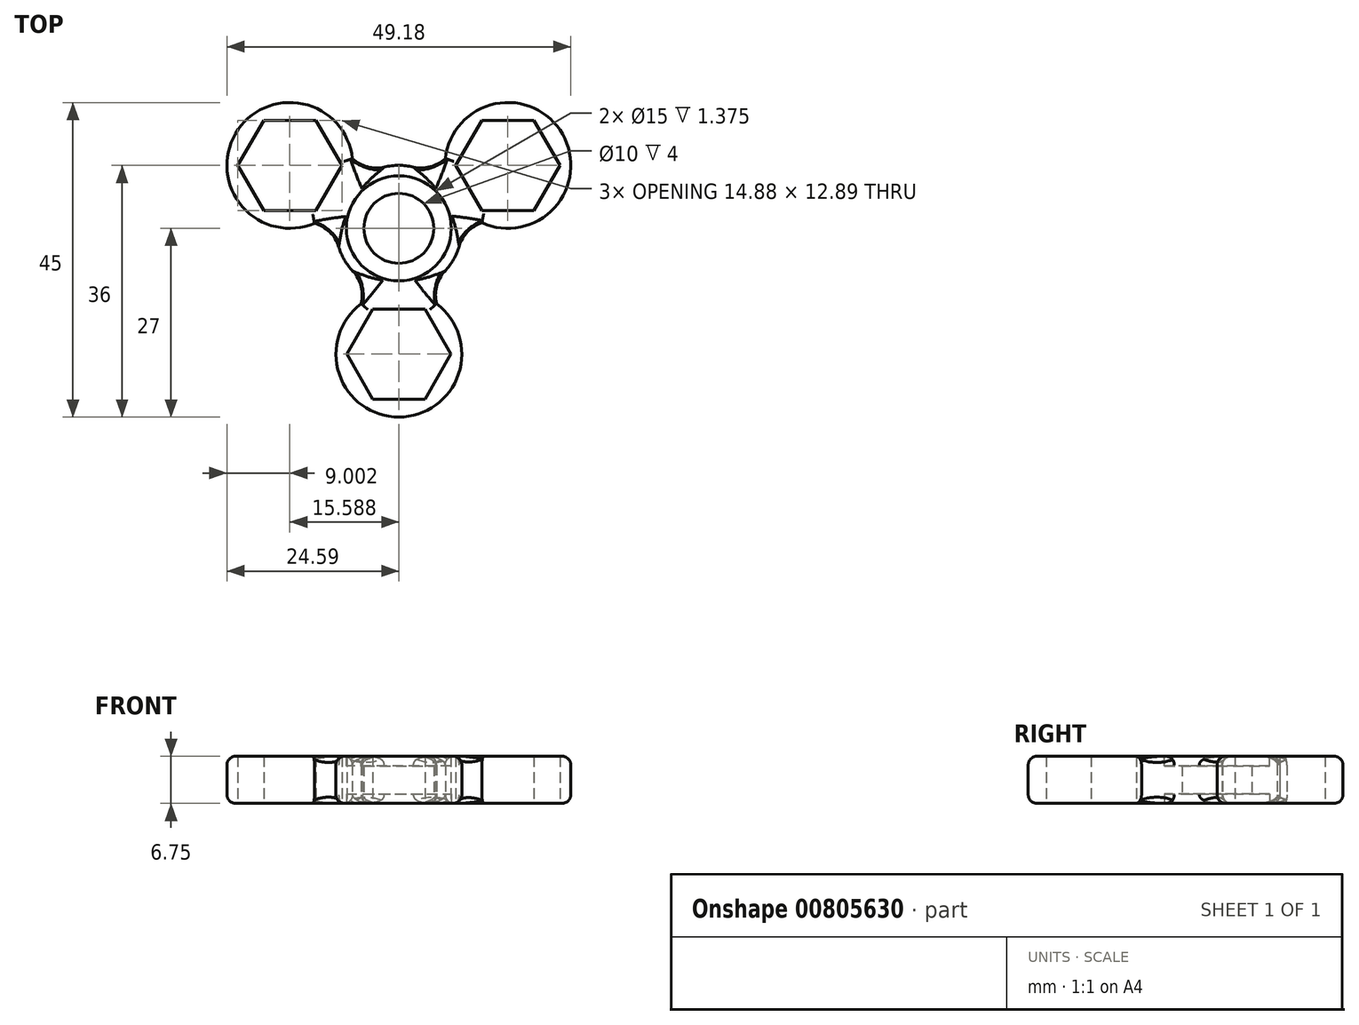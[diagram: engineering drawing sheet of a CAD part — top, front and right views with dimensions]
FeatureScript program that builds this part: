
annotation { "Feature Type Name" : "Feature", "Feature Type Description" : "" }
export const myFeature = defineFeature(function(context is Context, id is Id, definition is map)
    precondition{}
    {
        {
            var Q0;
            Q0=qCreatedBy(makeId("Top.planeOp"),FACE);
            var sketch = newSketch(context, id + "F0", { "sketchPlane" : qUnion([Q0])});
            skCircle(sketch, "E0.cCircle", {"center": v(0, 0) * mm, "radius": 9 * mm, "construction": true});
            skPoint(sketch, "E0.0.midPoint", {"position": v(0, 9) * mm});
            skCircle(sketch, "E1.cCircle", {"center": v(-15.59, 9) * mm, "radius": 6.44 * mm, "construction": true});
            skLineSegment(sketch, "E1.0", {"start": v(-19.3, 15.45) * mm, "end": v(-11.87, 15.45) * mm});
            skLineSegment(sketch, "E1.1", {"start": v(-11.87, 15.45) * mm, "end": v(-8.15, 9) * mm});
            skLineSegment(sketch, "E1.2", {"start": v(-8.15, 9) * mm, "end": v(-11.87, 2.55) * mm});
            skLineSegment(sketch, "E1.3", {"start": v(-11.87, 2.56) * mm, "end": v(-19.3, 2.56) * mm});
            skLineSegment(sketch, "E1.4", {"start": v(-19.3, 2.55) * mm, "end": v(-23.03, 9) * mm});
            skLineSegment(sketch, "E1.5", {"start": v(-23.03, 9) * mm, "end": v(-19.3, 15.45) * mm});
            skPoint(sketch, "E1.0.midPoint", {"position": v(-15.59, 15.45) * mm});
            skCircle(sketch, "E2.cCircle", {"center": v(15.59, 9) * mm, "radius": 6.44 * mm, "construction": true});
            skLineSegment(sketch, "E2.0", {"start": v(11.87, 2.55) * mm, "end": v(8.15, 9) * mm});
            skLineSegment(sketch, "E2.1", {"start": v(8.15, 9) * mm, "end": v(11.87, 15.45) * mm});
            skLineSegment(sketch, "E2.2", {"start": v(11.87, 15.45) * mm, "end": v(19.3, 15.45) * mm});
            skLineSegment(sketch, "E2.3", {"start": v(19.3, 15.45) * mm, "end": v(23.03, 9) * mm});
            skLineSegment(sketch, "E2.4", {"start": v(23.03, 9) * mm, "end": v(19.3, 2.56) * mm});
            skLineSegment(sketch, "E2.5", {"start": v(19.3, 2.56) * mm, "end": v(11.87, 2.55) * mm});
            skPoint(sketch, "E2.0.midPoint", {"position": v(10, 5.78) * mm});
            skCircle(sketch, "E3.cCircle", {"center": v(0, -18) * mm, "radius": 6.45 * mm, "construction": true});
            skLineSegment(sketch, "E3.0", {"start": v(-3.72, -11.56) * mm, "end": v(3.72, -11.56) * mm});
            skLineSegment(sketch, "E3.1", {"start": v(3.72, -11.55) * mm, "end": v(7.44, -18) * mm});
            skLineSegment(sketch, "E3.2", {"start": v(7.44, -18) * mm, "end": v(3.72, -24.44) * mm});
            skLineSegment(sketch, "E3.3", {"start": v(3.72, -24.45) * mm, "end": v(-3.72, -24.45) * mm});
            skLineSegment(sketch, "E3.4", {"start": v(-3.72, -24.45) * mm, "end": v(-7.44, -18) * mm});
            skLineSegment(sketch, "E3.5", {"start": v(-7.44, -18) * mm, "end": v(-3.72, -11.56) * mm});
            skPoint(sketch, "E3.0.midPoint", {"position": v(0, -11.56) * mm});
            skCircle(sketch, "E4", {"center": v(0, 0) * mm, "radius": 5 * mm});
            skLineSegment(sketch, "E5", {"start": v(-15.59, 9) * mm, "end": v(0, 0) * mm, "construction": true});
            skLineSegment(sketch, "E6", {"start": v(0, 0) * mm, "end": v(15.59, 9) * mm, "construction": true});
            skLineSegment(sketch, "E7", {"start": v(0, 0) * mm, "end": v(0, -18) * mm, "construction": true});
            skLineSegment(sketch, "E8", {"start": v(-20.06, 1.2) * mm, "end": v(0, 0) * mm, "construction": true});
            skLineSegment(sketch, "E9", {"start": v(0, 0) * mm, "end": v(-9, -18) * mm, "construction": true});
            skLineSegment(sketch, "E10", {"start": v(9, -18) * mm, "end": v(0, 0) * mm, "construction": true});
            skLineSegment(sketch, "E11", {"start": v(0, 0) * mm, "end": v(20.36, 1.37) * mm, "construction": true});
            skLineSegment(sketch, "E12", {"start": v(11.2, 16.86) * mm, "end": v(0, 0) * mm, "construction": true});
            skLineSegment(sketch, "E13", {"start": v(0, 0) * mm, "end": v(-11.22, 16.87) * mm, "construction": true});
            skLineSegment(sketch, "E14", {"start": v(-12.07, 0.72) * mm, "end": v(-8.98, 0.53) * mm});
            skLineSegment(sketch, "E15", {"start": v(-4.02, -8.05) * mm, "end": v(-5.4, -10.8) * mm});
            skLineSegment(sketch, "E16", {"start": v(4.02, -8.05) * mm, "end": v(5.4, -10.8) * mm});
            skLineSegment(sketch, "E17", {"start": v(8.98, 0.6) * mm, "end": v(11.88, 0.8) * mm});
            skLineSegment(sketch, "E18", {"start": v(4.98, 7.5) * mm, "end": v(6.64, 10) * mm});
            skLineSegment(sketch, "E19", {"start": v(-4.98, 7.5) * mm, "end": v(-6.64, 9.99) * mm});
            skArc(sketch, "E20", {"start": v(4.98, 7.5) * mm, "mid": v(0, 9) * mm, "end": v(-4.98, 7.5) * mm});
            skArc(sketch, "E21", {"start": v(8.98, 0.6) * mm, "mid": v(7.81, -4.47) * mm, "end": v(4.02, -8.05) * mm});
            skArc(sketch, "E22", {"start": v(-4.02, -8.05) * mm, "mid": v(-7.8, -4.5) * mm, "end": v(-8.98, 0.53) * mm});
            skArc(sketch, "E23", {"start": v(-6.64, 9.99) * mm, "mid": v(-23.36, 13.55) * mm, "end": v(-12.07, 0.72) * mm});
            skArc(sketch, "E24", {"start": v(6.64, 10) * mm, "mid": v(23.4, 13.45) * mm, "end": v(11.88, 0.8) * mm});
            skArc(sketch, "E25", {"start": v(5.4, -10.8) * mm, "mid": v(0, -27) * mm, "end": v(-5.4, -10.8) * mm});
            skSolve(sketch);
        }
        {
            var Q0;
            Q0=qSketchRegion(id+"F0",true);
            extrude(context, id + "F1", {"entities" : qUnion([Q0]), "depth" : 6.75 * mm, "offsetDistance" : 25 * mm});
        }
        {
            var Q0;
            Q0=makeQuery(id+"F1.opExtrude","CAP_FACE",FACE,{"disambiguationData":[OSD([sQuery(id+"F0.wireOp",EDGE,"E1.0"),sQuery(id+"F0.wireOp",EDGE,"E1.1"),sQuery(id+"F0.wireOp",EDGE,"E1.2"),sQuery(id+"F0.wireOp",EDGE,"E1.3"),sQuery(id+"F0.wireOp",EDGE,"E1.4"),sQuery(id+"F0.wireOp",EDGE,"E1.5"),sQuery(id+"F0.wireOp",EDGE,"E2.0"),sQuery(id+"F0.wireOp",EDGE,"E2.1"),sQuery(id+"F0.wireOp",EDGE,"E2.2"),sQuery(id+"F0.wireOp",EDGE,"E2.3"),sQuery(id+"F0.wireOp",EDGE,"E2.4"),sQuery(id+"F0.wireOp",EDGE,"E2.5"),sQuery(id+"F0.wireOp",EDGE,"E3.0"),sQuery(id+"F0.wireOp",EDGE,"E3.1"),sQuery(id+"F0.wireOp",EDGE,"E3.2"),sQuery(id+"F0.wireOp",EDGE,"E3.3"),sQuery(id+"F0.wireOp",EDGE,"E3.4"),sQuery(id+"F0.wireOp",EDGE,"E3.5"),sQuery(id+"F0.wireOp",EDGE,"E4"),sQuery(id+"F0.wireOp",EDGE,"E14"),sQuery(id+"F0.wireOp",EDGE,"E15"),sQuery(id+"F0.wireOp",EDGE,"E16"),sQuery(id+"F0.wireOp",EDGE,"E17"),sQuery(id+"F0.wireOp",EDGE,"E18"),sQuery(id+"F0.wireOp",EDGE,"E19"),sQuery(id+"F0.wireOp",EDGE,"E20"),sQuery(id+"F0.wireOp",EDGE,"E21"),sQuery(id+"F0.wireOp",EDGE,"E22"),sQuery(id+"F0.wireOp",EDGE,"E23"),sQuery(id+"F0.wireOp",EDGE,"E24"),sQuery(id+"F0.wireOp",EDGE,"E25")])],"isStart":false});
            var sketch = newSketch(context, id + "F2", { "sketchPlane" : qUnion([Q0])});
            skCircle(sketch, "E26", {"center": v(0, 0) * mm, "radius": 7.5 * mm});
            skSolve(sketch);
        }
        {
            var Q0;
            Q0=qSketchRegion(id+"F2",true);
            extrude(context, id + "F3", {"entities" : qUnion([Q0]), "operationType" : NewBodyOperationType.REMOVE, "oppositeDirection" : true, "depth" : 1.38 * mm, "offsetDistance" : 25 * mm});
        }
        {
            var Q0;
            Q0=makeQuery(id+"F1.opExtrude","CAP_FACE",FACE,{"disambiguationData":[OSD([sQuery(id+"F0.wireOp",EDGE,"E1.0"),sQuery(id+"F0.wireOp",EDGE,"E1.1"),sQuery(id+"F0.wireOp",EDGE,"E1.2"),sQuery(id+"F0.wireOp",EDGE,"E1.3"),sQuery(id+"F0.wireOp",EDGE,"E1.4"),sQuery(id+"F0.wireOp",EDGE,"E1.5"),sQuery(id+"F0.wireOp",EDGE,"E2.0"),sQuery(id+"F0.wireOp",EDGE,"E2.1"),sQuery(id+"F0.wireOp",EDGE,"E2.2"),sQuery(id+"F0.wireOp",EDGE,"E2.3"),sQuery(id+"F0.wireOp",EDGE,"E2.4"),sQuery(id+"F0.wireOp",EDGE,"E2.5"),sQuery(id+"F0.wireOp",EDGE,"E3.0"),sQuery(id+"F0.wireOp",EDGE,"E3.1"),sQuery(id+"F0.wireOp",EDGE,"E3.2"),sQuery(id+"F0.wireOp",EDGE,"E3.3"),sQuery(id+"F0.wireOp",EDGE,"E3.4"),sQuery(id+"F0.wireOp",EDGE,"E3.5"),sQuery(id+"F0.wireOp",EDGE,"E4"),sQuery(id+"F0.wireOp",EDGE,"E14"),sQuery(id+"F0.wireOp",EDGE,"E15"),sQuery(id+"F0.wireOp",EDGE,"E16"),sQuery(id+"F0.wireOp",EDGE,"E17"),sQuery(id+"F0.wireOp",EDGE,"E18"),sQuery(id+"F0.wireOp",EDGE,"E19"),sQuery(id+"F0.wireOp",EDGE,"E20"),sQuery(id+"F0.wireOp",EDGE,"E21"),sQuery(id+"F0.wireOp",EDGE,"E22"),sQuery(id+"F0.wireOp",EDGE,"E23"),sQuery(id+"F0.wireOp",EDGE,"E24"),sQuery(id+"F0.wireOp",EDGE,"E25")])],"isStart":true});
            var sketch = newSketch(context, id + "F4", { "sketchPlane" : qUnion([Q0])});
            skCircle(sketch, "E27", {"center": v(0, 0) * mm, "radius": 7.5 * mm});
            skSolve(sketch);
        }
        {
            var Q0;
            Q0=qSketchRegion(id+"F4",true);
            extrude(context, id + "F5", {"entities" : qUnion([Q0]), "operationType" : NewBodyOperationType.REMOVE, "oppositeDirection" : true, "depth" : 1.38 * mm, "offsetDistance" : 25 * mm});
        }
        {
            var Q0;
            Q0=makeQuery(id+"F1.opExtrude","CAP_EDGE",EDGE,{"disambiguationData":[OSD([sQuery(id+"F0.wireOp",EDGE,"E23")])],"isStart":false});
            var Q1;
            Q1=makeQuery(id+"F1.opExtrude","CAP_EDGE",EDGE,{"disambiguationData":[OSD([sQuery(id+"F0.wireOp",EDGE,"E19")])],"isStart":false});
            var Q2;
            Q2=makeQuery(id+"F1.opExtrude","CAP_EDGE",EDGE,{"disambiguationData":[OSD([sQuery(id+"F0.wireOp",EDGE,"E20")])],"isStart":false});
            var Q3;
            Q3=makeQuery(id+"F1.opExtrude","CAP_EDGE",EDGE,{"disambiguationData":[OSD([sQuery(id+"F0.wireOp",EDGE,"E18")])],"isStart":false});
            var Q4;
            Q4=makeQuery(id+"F1.opExtrude","CAP_EDGE",EDGE,{"disambiguationData":[OSD([sQuery(id+"F0.wireOp",EDGE,"E24")])],"isStart":false});
            var Q5;
            Q5=makeQuery(id+"F1.opExtrude","CAP_EDGE",EDGE,{"disambiguationData":[OSD([sQuery(id+"F0.wireOp",EDGE,"E17")])],"isStart":false});
            var Q6;
            Q6=makeQuery(id+"F1.opExtrude","CAP_EDGE",EDGE,{"disambiguationData":[OSD([sQuery(id+"F0.wireOp",EDGE,"E21")])],"isStart":false});
            var Q7;
            Q7=makeQuery(id+"F1.opExtrude","CAP_EDGE",EDGE,{"disambiguationData":[OSD([sQuery(id+"F0.wireOp",EDGE,"E16")])],"isStart":false});
            var Q8;
            Q8=makeQuery(id+"F1.opExtrude","CAP_EDGE",EDGE,{"disambiguationData":[OSD([sQuery(id+"F0.wireOp",EDGE,"E25")])],"isStart":false});
            var Q9;
            Q9=makeQuery(id+"F1.opExtrude","CAP_EDGE",EDGE,{"disambiguationData":[OSD([sQuery(id+"F0.wireOp",EDGE,"E15")])],"isStart":false});
            var Q10;
            Q10=makeQuery(id+"F1.opExtrude","CAP_EDGE",EDGE,{"disambiguationData":[OSD([sQuery(id+"F0.wireOp",EDGE,"E22")])],"isStart":false});
            var Q11;
            Q11=makeQuery(id+"F1.opExtrude","CAP_EDGE",EDGE,{"disambiguationData":[OSD([sQuery(id+"F0.wireOp",EDGE,"E14")])],"isStart":false});
            var Q12;
            Q12=makeQuery(id+"F1.opExtrude","CAP_EDGE",EDGE,{"disambiguationData":[OSD([sQuery(id+"F0.wireOp",EDGE,"E20")])],"isStart":true});
            var Q13;
            Q13=makeQuery(id+"F1.opExtrude","CAP_EDGE",EDGE,{"disambiguationData":[OSD([sQuery(id+"F0.wireOp",EDGE,"E19")])],"isStart":true});
            var Q14;
            Q14=makeQuery(id+"F1.opExtrude","CAP_EDGE",EDGE,{"disambiguationData":[OSD([sQuery(id+"F0.wireOp",EDGE,"E23")])],"isStart":true});
            var Q15;
            Q15=makeQuery(id+"F1.opExtrude","CAP_EDGE",EDGE,{"disambiguationData":[OSD([sQuery(id+"F0.wireOp",EDGE,"E14")])],"isStart":true});
            var Q16;
            Q16=makeQuery(id+"F1.opExtrude","CAP_EDGE",EDGE,{"disambiguationData":[OSD([sQuery(id+"F0.wireOp",EDGE,"E22")])],"isStart":true});
            var Q17;
            Q17=makeQuery(id+"F1.opExtrude","CAP_EDGE",EDGE,{"disambiguationData":[OSD([sQuery(id+"F0.wireOp",EDGE,"E15")])],"isStart":true});
            var Q18;
            Q18=makeQuery(id+"F1.opExtrude","CAP_EDGE",EDGE,{"disambiguationData":[OSD([sQuery(id+"F0.wireOp",EDGE,"E25")])],"isStart":true});
            var Q19;
            Q19=makeQuery(id+"F1.opExtrude","CAP_EDGE",EDGE,{"disambiguationData":[OSD([sQuery(id+"F0.wireOp",EDGE,"E16")])],"isStart":true});
            var Q20;
            Q20=makeQuery(id+"F1.opExtrude","CAP_EDGE",EDGE,{"disambiguationData":[OSD([sQuery(id+"F0.wireOp",EDGE,"E21")])],"isStart":true});
            var Q21;
            Q21=makeQuery(id+"F1.opExtrude","CAP_EDGE",EDGE,{"disambiguationData":[OSD([sQuery(id+"F0.wireOp",EDGE,"E17")])],"isStart":true});
            var Q22;
            Q22=makeQuery(id+"F1.opExtrude","CAP_EDGE",EDGE,{"disambiguationData":[OSD([sQuery(id+"F0.wireOp",EDGE,"E24")])],"isStart":true});
            var Q23;
            Q23=makeQuery(id+"F1.opExtrude","CAP_EDGE",EDGE,{"disambiguationData":[OSD([sQuery(id+"F0.wireOp",EDGE,"E18")])],"isStart":true});
            fillet(context, id + "F6", {"entities" : qUnion([Q0, Q1, Q2, Q3, Q4, Q5, Q6, Q7, Q8, Q9, Q10, Q11, Q12, Q13, Q14, Q15, Q16, Q17, Q18, Q19, Q20, Q21, Q22, Q23]), "radius" : 1.25 * mm, "tangentPropagation" : true, "allowEdgeOverflow" : false});
        }
        {
            var Q0;
            Q0=makeQuery(id+"F1.opExtrude","SWEPT_EDGE",EDGE,{"disambiguationData":[OSD([sQuery(id+"F0.wireOp",EDGE,"E16"),sQuery(id+"F0.wireOp",EDGE,"E21")])]});
            var Q1;
            Q1=makeQuery(id+"F1.opExtrude","SWEPT_EDGE",EDGE,{"disambiguationData":[OSD([sQuery(id+"F0.wireOp",EDGE,"E17"),sQuery(id+"F0.wireOp",EDGE,"E21")])]});
            var Q2;
            Q2=makeQuery(id+"F1.opExtrude","SWEPT_EDGE",EDGE,{"disambiguationData":[OSD([sQuery(id+"F0.wireOp",EDGE,"E18"),sQuery(id+"F0.wireOp",EDGE,"E20")])]});
            var Q3;
            Q3=makeQuery(id+"F1.opExtrude","SWEPT_EDGE",EDGE,{"disambiguationData":[OSD([sQuery(id+"F0.wireOp",EDGE,"E19"),sQuery(id+"F0.wireOp",EDGE,"E20")])]});
            var Q4;
            Q4=makeQuery(id+"F1.opExtrude","SWEPT_EDGE",EDGE,{"disambiguationData":[OSD([sQuery(id+"F0.wireOp",EDGE,"E15"),sQuery(id+"F0.wireOp",EDGE,"E22")])]});
            var Q5;
            Q5=makeQuery(id+"F1.opExtrude","SWEPT_EDGE",EDGE,{"disambiguationData":[OSD([sQuery(id+"F0.wireOp",EDGE,"E14"),sQuery(id+"F0.wireOp",EDGE,"E22")])]});
            fillet(context, id + "F7", {"entities" : qUnion([Q0, Q1, Q2, Q3, Q4, Q5]), "radius" : 5 * mm, "tangentPropagation" : true, "allowEdgeOverflow" : false});
        }
    });
